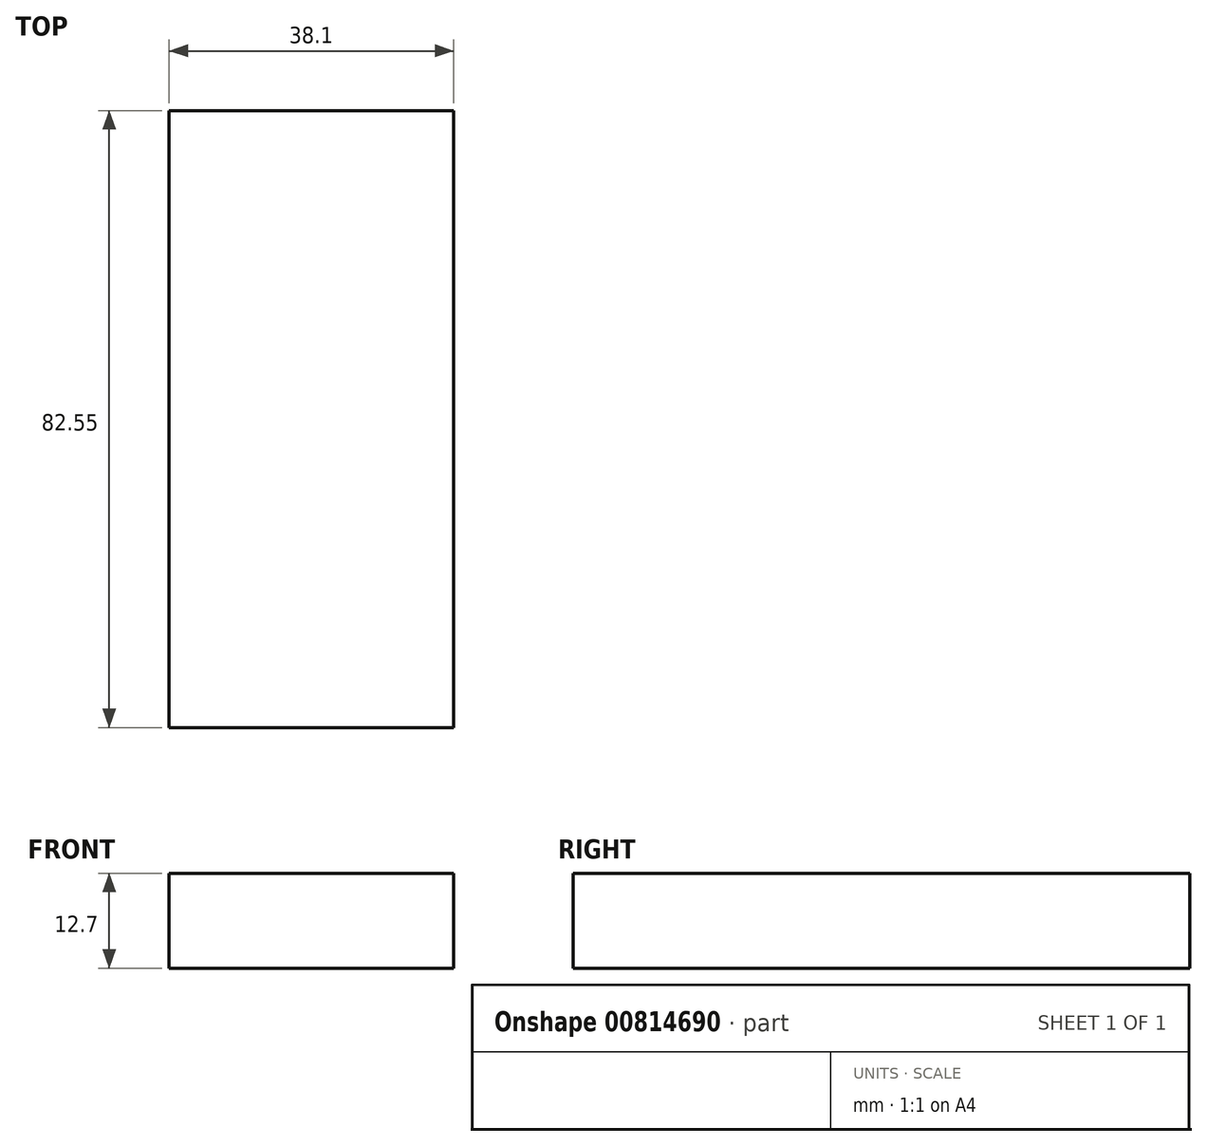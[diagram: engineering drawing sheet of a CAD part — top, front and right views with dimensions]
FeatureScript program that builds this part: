
annotation { "Feature Type Name" : "Feature", "Feature Type Description" : "" }
export const myFeature = defineFeature(function(context is Context, id is Id, definition is map)
    precondition{}
    {
        {
            var Q0;
            Q0=qCreatedBy(makeId("Top.planeOp"),FACE);
            var sketch = newSketch(context, id + "F0", { "sketchPlane" : qUnion([Q0])});
            skLineSegment(sketch, "E0.bottom", {"start": v(0, 0) * mm, "end": v(38.1, 0) * mm});
            skLineSegment(sketch, "E0.top", {"start": v(0, 82.55) * mm, "end": v(38.1, 82.55) * mm});
            skLineSegment(sketch, "E0.left", {"start": v(0, 0) * mm, "end": v(0, 82.55) * mm});
            skLineSegment(sketch, "E0.right", {"start": v(38.1, 0) * mm, "end": v(38.1, 82.55) * mm});
            skSolve(sketch);
        }
        {
            var Q0;
            Q0=qSketchRegion(id+"F0",true);
            extrude(context, id + "F1", {"entities" : qUnion([Q0]), "depth" : 12.7 * mm, "offsetDistance" : 25.4 * mm});
        }
    });
